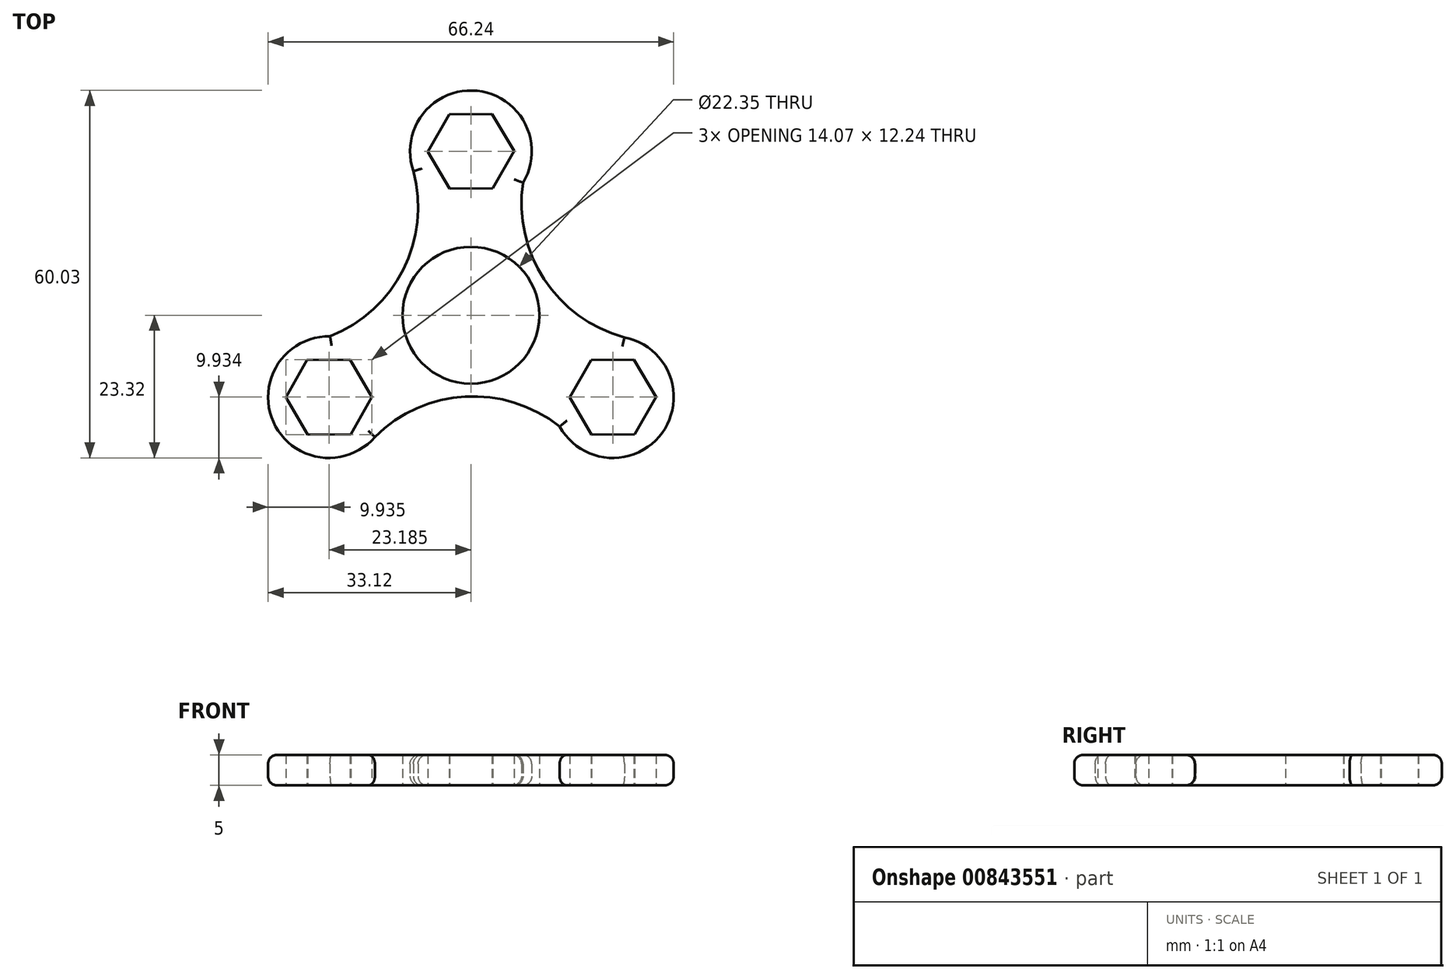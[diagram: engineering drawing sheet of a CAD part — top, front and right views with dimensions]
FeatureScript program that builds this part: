
annotation { "Feature Type Name" : "Feature", "Feature Type Description" : "" }
export const myFeature = defineFeature(function(context is Context, id is Id, definition is map)
    precondition{}
    {
        {
            var Q0;
            Q0=qCreatedBy(makeId("Top.planeOp"),FACE);
            var sketch = newSketch(context, id + "F0", { "sketchPlane" : qUnion([Q0])});
            skCircle(sketch, "E0", {"center": v(0, 0) * mm, "radius": 11.18 * mm});
            skArc(sketch, "E1.cCircle", {"start": v(-5.3, 29.78) * mm, "mid": v(-6.1, 26.72) * mm, "end": v(-5.25, 23.68) * mm, "construction": true});
            skLineSegment(sketch, "E1.0", {"start": v(-3.47, 20.65) * mm, "end": v(-7.03, 26.71) * mm});
            skLineSegment(sketch, "E1.1", {"start": v(-7.03, 26.71) * mm, "end": v(-3.57, 32.84) * mm});
            skLineSegment(sketch, "E1.2", {"start": v(-3.57, 32.84) * mm, "end": v(3.47, 32.9) * mm});
            skLineSegment(sketch, "E1.3", {"start": v(3.47, 32.9) * mm, "end": v(7.03, 26.83) * mm});
            skLineSegment(sketch, "E1.4", {"start": v(7.03, 26.83) * mm, "end": v(3.57, 20.7) * mm});
            skLineSegment(sketch, "E1.5", {"start": v(3.57, 20.7) * mm, "end": v(-3.47, 20.65) * mm});
            skPoint(sketch, "E1.0.midPoint", {"position": v(-5.25, 23.68) * mm});
            skArc(sketch, "E2", {"start": v(8.52, 21.65) * mm, "mid": v(1.04, 36.65) * mm, "end": v(-9.4, 23.53) * mm});
            skArc(sketch, "E3.1.0", {"start": v(-23, -3.45) * mm, "mid": v(-32.26, -17.43) * mm, "end": v(-15.68, -19.9) * mm});
            skLineSegment(sketch, "E3.1.1", {"start": v(-19.72, -7.27) * mm, "end": v(-16.15, -13.33) * mm});
            skLineSegment(sketch, "E3.1.2", {"start": v(-16.15, -13.33) * mm, "end": v(-19.62, -19.45) * mm});
            skLineSegment(sketch, "E3.1.3", {"start": v(-19.62, -19.45) * mm, "end": v(-26.65, -19.5) * mm});
            skLineSegment(sketch, "E3.1.4", {"start": v(-26.65, -19.5) * mm, "end": v(-30.22, -13.44) * mm});
            skLineSegment(sketch, "E3.1.5", {"start": v(-30.22, -13.44) * mm, "end": v(-26.75, -7.32) * mm});
            skLineSegment(sketch, "E3.1.6", {"start": v(-26.75, -7.32) * mm, "end": v(-19.72, -7.27) * mm});
            skArc(sketch, "E3.2.0", {"start": v(14.5, -18.2) * mm, "mid": v(31.23, -19.22) * mm, "end": v(25.07, -3.63) * mm});
            skLineSegment(sketch, "E3.2.1", {"start": v(16.15, -13.44) * mm, "end": v(19.62, -7.32) * mm});
            skLineSegment(sketch, "E3.2.2", {"start": v(19.62, -7.32) * mm, "end": v(26.65, -7.27) * mm});
            skLineSegment(sketch, "E3.2.3", {"start": v(26.65, -7.27) * mm, "end": v(30.22, -13.33) * mm});
            skLineSegment(sketch, "E3.2.4", {"start": v(30.22, -13.33) * mm, "end": v(26.75, -19.45) * mm});
            skLineSegment(sketch, "E3.2.5", {"start": v(26.75, -19.45) * mm, "end": v(19.72, -19.5) * mm});
            skLineSegment(sketch, "E3.2.6", {"start": v(19.72, -19.5) * mm, "end": v(16.15, -13.44) * mm});
            skArc(sketch, "E4", {"start": v(9.94, 26.83) * mm, "mid": v(10.63, 8.19) * mm, "end": v(25.07, -3.63) * mm});
            skArc(sketch, "E5.1.0", {"start": v(-28.2, -4.8) * mm, "mid": v(-12.4, 5.12) * mm, "end": v(-9.4, 23.53) * mm});
            skArc(sketch, "E5.2.0", {"start": v(18.27, -22.02) * mm, "mid": v(1.77, -13.3) * mm, "end": v(-15.68, -19.9) * mm});
            skLineSegment(sketch, "E6.trimOffspring", {"start": v(9.68, 5.59) * mm, "end": v(11.6, 6.7) * mm, "construction": true});
            skLineSegment(sketch, "E7.trimOffspring", {"start": v(10.2, 9.1) * mm, "end": v(12.62, 4.91) * mm, "construction": true});
            skLineSegment(sketch, "E8.trimOffspring", {"start": v(18.22, -4.78) * mm, "end": v(19.68, -7.32) * mm, "construction": true});
            skSolve(sketch);
        }
        {
            var Q0;
            Q0 = qSketchRegion(id + "F0", true);
            extrude(context, id + "F1", {"entities" : qUnion([Q0]), "depth" : 5 * mm, "offsetDistance" : 25 * mm});
        }
        {
            var Q0;
            Q0=makeQuery(id+"F1.opExtrude","CAP_EDGE",EDGE,{"disambiguationData":[OSD([sQuery(id+"F0.wireOp",EDGE,"E5.2.0")])],"isStart":false});
            var Q1;
            Q1=makeQuery(id+"F1.opExtrude","CAP_EDGE",EDGE,{"disambiguationData":[OSD([sQuery(id+"F0.wireOp",EDGE,"E3.1.0")])],"isStart":false});
            var Q2;
            Q2=makeQuery(id+"F1.opExtrude","CAP_EDGE",EDGE,{"disambiguationData":[OSD([sQuery(id+"F0.wireOp",EDGE,"E5.1.0")])],"isStart":false});
            var Q3;
            Q3=makeQuery(id+"F1.opExtrude","CAP_EDGE",EDGE,{"disambiguationData":[OSD([sQuery(id+"F0.wireOp",EDGE,"E2")])],"isStart":false});
            var Q4;
            Q4=makeQuery(id+"F1.opExtrude","CAP_EDGE",EDGE,{"disambiguationData":[OSD([sQuery(id+"F0.wireOp",EDGE,"E3.2.0")])],"isStart":false});
            var Q5;
            Q5=makeQuery(id+"F1.opExtrude","CAP_EDGE",EDGE,{"disambiguationData":[OSD([sQuery(id+"F0.wireOp",EDGE,"E4")])],"isStart":false});
            fillet(context, id + "F2", {"entities" : qUnion([Q0, Q1, Q2, Q3, Q4, Q5]), "radius" : 1.5 * mm, "tangentPropagation" : true, "allowEdgeOverflow" : false});
        }
        {
            var Q0;
            Q0=makeQuery(id+"F1.opExtrude","CAP_EDGE",EDGE,{"disambiguationData":[OSD([sQuery(id+"F0.wireOp",EDGE,"E3.1.0")])],"isStart":true});
            var Q1;
            Q1=makeQuery(id+"F1.opExtrude","CAP_EDGE",EDGE,{"disambiguationData":[OSD([sQuery(id+"F0.wireOp",EDGE,"E5.2.0")])],"isStart":true});
            var Q2;
            Q2=makeQuery(id+"F1.opExtrude","CAP_EDGE",EDGE,{"disambiguationData":[OSD([sQuery(id+"F0.wireOp",EDGE,"E3.2.0")])],"isStart":true});
            var Q3;
            Q3=makeQuery(id+"F1.opExtrude","CAP_EDGE",EDGE,{"disambiguationData":[OSD([sQuery(id+"F0.wireOp",EDGE,"E4")])],"isStart":true});
            var Q4;
            Q4=makeQuery(id+"F1.opExtrude","CAP_EDGE",EDGE,{"disambiguationData":[OSD([sQuery(id+"F0.wireOp",EDGE,"E2")])],"isStart":true});
            var Q5;
            Q5=makeQuery(id+"F1.opExtrude","CAP_EDGE",EDGE,{"disambiguationData":[OSD([sQuery(id+"F0.wireOp",EDGE,"E5.1.0")])],"isStart":true});
            fillet(context, id + "F3", {"entities" : qUnion([Q0, Q1, Q2, Q3, Q4, Q5]), "radius" : 1.5 * mm, "tangentPropagation" : true, "allowEdgeOverflow" : false});
        }
    });
